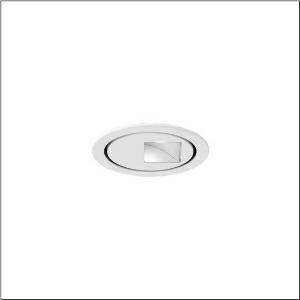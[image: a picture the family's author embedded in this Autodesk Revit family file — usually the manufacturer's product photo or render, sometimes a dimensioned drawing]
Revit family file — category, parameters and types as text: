
# Revit family: lunis_11_micro_round_51dj11cd1wg21
name_source: partatom
category: Lighting Fixtures
units: mm (PartAtom-declared; Revit-internal decimal feet)

## family parameters
Cut with Voids When Loaded = No
Host = Face
Light Source = No
Part Type = Normal
Room Calculation Point = No
Round Connector Dimension = Use Diameter
Shared = No

## types (1)
- Lunis 11 micro round (1 x LED 4000K / CRI = 80 (unbekannt), 1400 lm, 4000K)
    Apparent Load = 20 VA
    CIE Flux Codes = 42 75 96 100 100
    Color Rendering = 80
    Color Temperature = 4000K
    Default Elevation = 1800 mm
    Description = Lunis 11 micro round, downlight, light control with wallwasher, of highly reflective aluminium, highly specular, light emission: direct distribution, LED rated luminous flux: 1.400lm, light colour: 840, control gear: ECG, with terminal, 5-pole, mains connection: 220..230V, AC/DC, 0/50..60Hz, LED module, luminaire module, of aluminium, highly specular, white, diameter: 114mm, clamping range: 1..40mm, recessing ring, of plastic, traffic white (RAL 9016), protection rating (complete): IP20, insulation class (complete): insulation class II (safety insulation), certification: CE, permissible ambient temperature for indoor applications: 0..+35°C, packaging unit: 1 piece
    Height = 0 mm  [stored 0 ft]
    Lamp = 1 x LED 4000K / CRI >= 80 (unbekannt)
    Lamp Light Flux = 1400 lm
    Lamp count = 1
    Length = 114 mm
    Luminous efficacy = 71 lm/W
    Manufacturer = Siteco
    ModVariant = No
    Model = 51DJ11CD1WG21
    Mounting Place = Ceiling
    Mounting Type = Recessed
    Number of Poles = 1
    OnlyDefault = Yes
    Power Factor = 1
    Product Name = Lunis 11 micro round
    Product group = downlight | ceiling recessed
    ProductGroupID = 402
    Protection Class = Protection class II
    Protection Degree = IP 20
    RLX_Detail_Level = 1
    RlxData = <blob elided: 41049 chars, md5=e7b741cb>
    Socket = socket
    Standby Power = 0 W
    System Light Flux = 1400 lm
    System Power = 20 W
    Type Comments = Product without accessories
    Type Image = l_1004773.jpg
    URL = http://relux.com
    VarID = ---
    Voltage = 0 V
    Weight = 0.00 kg
    Width = 114 mm

note: [stored X ft] marks values corroborated as IEEE doubles in the binary element streams (Revit-internal decimal feet)

## geometry (parser evidence)
native form markers: Blend x4, Sweep x9
no freeform markers — native parametric forms only
